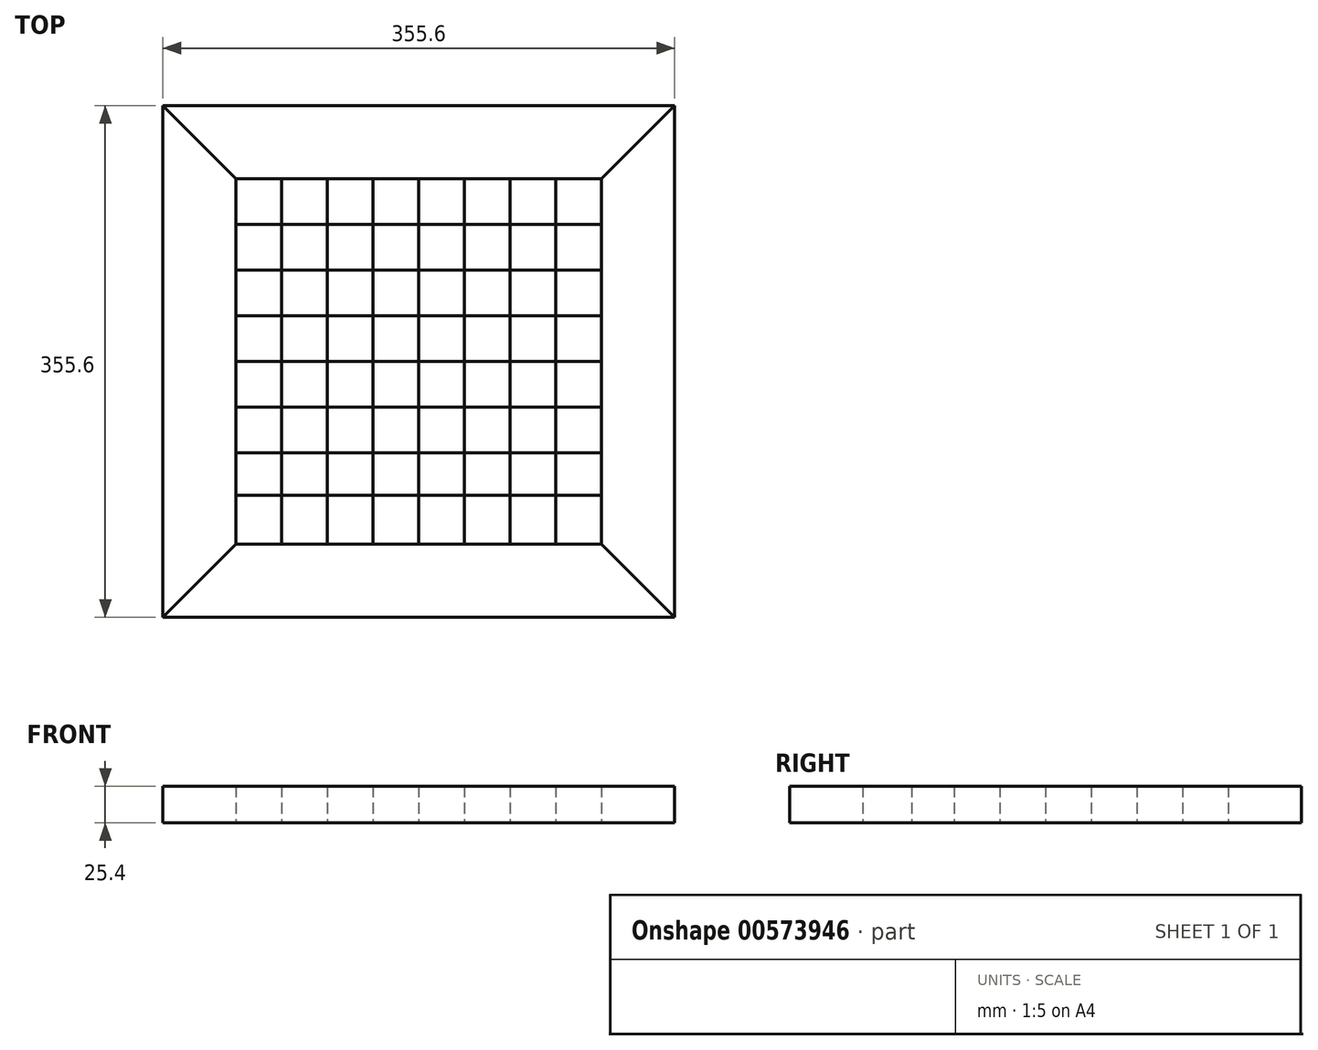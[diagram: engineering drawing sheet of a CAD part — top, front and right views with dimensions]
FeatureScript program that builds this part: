
annotation { "Feature Type Name" : "Feature", "Feature Type Description" : "" }
export const myFeature = defineFeature(function(context is Context, id is Id, definition is map)
    precondition{}
    {
        {
            var Q0;
            Q0=qCreatedBy(makeId("Top.planeOp"),FACE);
            var sketch = newSketch(context, id + "F0", { "sketchPlane" : qUnion([Q0])});
            skLineSegment(sketch, "E0.bottom", {"start": v(-177.8, -177.8) * mm, "end": v(177.8, -177.8) * mm});
            skLineSegment(sketch, "E0.top", {"start": v(-177.8, 177.8) * mm, "end": v(177.8, 177.8) * mm});
            skLineSegment(sketch, "E0.left", {"start": v(-177.8, -177.8) * mm, "end": v(-177.8, 177.8) * mm});
            skLineSegment(sketch, "E0.right", {"start": v(177.8, -177.8) * mm, "end": v(177.8, 177.8) * mm});
            skPoint(sketch, "E0.middle", {"position": v(0, 0) * mm});
            skLineSegment(sketch, "E1", {"start": v(-177.8, 177.8) * mm, "end": v(-127, 127) * mm});
            skLineSegment(sketch, "E2", {"start": v(-177.8, -177.8) * mm, "end": v(-127, -127) * mm});
            skLineSegment(sketch, "E3", {"start": v(-127, 127) * mm, "end": v(-127, -127) * mm});
            skLineSegment(sketch, "E4", {"start": v(-127, 127) * mm, "end": v(127, 127) * mm});
            skLineSegment(sketch, "E5", {"start": v(127, 127) * mm, "end": v(127, -127) * mm});
            skLineSegment(sketch, "E6", {"start": v(127, -127) * mm, "end": v(-127, -127) * mm});
            skLineSegment(sketch, "E7.trimOffspring", {"start": v(127, -127) * mm, "end": v(177.8, -177.8) * mm});
            skLineSegment(sketch, "E8.trimOffspring", {"start": v(127, 127) * mm, "end": v(177.8, 177.8) * mm});
            skLineSegment(sketch, "E9", {"start": v(-95.25, 127) * mm, "end": v(-95.25, -127) * mm});
            skLineSegment(sketch, "E10", {"start": v(-63.5, 127) * mm, "end": v(-63.5, -127) * mm});
            skLineSegment(sketch, "E11", {"start": v(-31.75, 127) * mm, "end": v(-31.75, -127) * mm});
            skLineSegment(sketch, "E12", {"start": v(0, 127) * mm, "end": v(0, -127) * mm});
            skLineSegment(sketch, "E13", {"start": v(31.75, 127) * mm, "end": v(31.75, -127) * mm});
            skLineSegment(sketch, "E14", {"start": v(63.5, 127) * mm, "end": v(63.5, -127) * mm});
            skLineSegment(sketch, "E15", {"start": v(95.25, 127) * mm, "end": v(95.25, -127) * mm});
            skLineSegment(sketch, "E16", {"start": v(-127, 95.25) * mm, "end": v(127, 95.25) * mm});
            skLineSegment(sketch, "E17", {"start": v(-127, 63.5) * mm, "end": v(127, 63.5) * mm});
            skLineSegment(sketch, "E18", {"start": v(-127, 31.75) * mm, "end": v(127, 31.75) * mm});
            skLineSegment(sketch, "E19", {"start": v(-127, 0) * mm, "end": v(127, 0) * mm});
            skLineSegment(sketch, "E20", {"start": v(-127, -31.75) * mm, "end": v(127, -31.75) * mm});
            skLineSegment(sketch, "E21", {"start": v(-127, -63.5) * mm, "end": v(127, -63.5) * mm});
            skLineSegment(sketch, "E22", {"start": v(127, -92.97) * mm, "end": v(-127, -92.97) * mm});
            skSolve(sketch);
        }
        {
            var Q0;
            Q0=makeQuery(id+"F0.imprint","IMPRINT",FACE,{"disambiguationData":[TD([[makeQuery(id+"F0.imprint","IMPRINT",EDGE,{"derivedFrom":sQuery(id+"F0.wireOp",EDGE,"E0.top")}),-1.0]])]});
            var Q1;
            Q1=makeQuery(id+"F0.imprint","IMPRINT",FACE,{"disambiguationData":[TD([[makeQuery(id+"F0.imprint","IMPRINT",EDGE,{"derivedFrom":sQuery(id+"F0.wireOp",EDGE,"E0.bottom")}),1.0]])]});
            extrude(context, id + "F1", {"entities" : qUnion([Q0, Q1]), "depth" : 25.4 * mm, "offsetDistance" : 25.4 * mm});
        }
        {
            var Q0;
            Q0=makeQuery(id+"F0.imprint","IMPRINT",FACE,{"disambiguationData":[TD([[makeQuery(id+"F0.imprint","IMPRINT",EDGE,{"derivedFrom":sQuery(id+"F0.wireOp",EDGE,"E0.left")}),-1.0]])]});
            var Q1;
            Q1=makeQuery(id+"F0.imprint","IMPRINT",FACE,{"disambiguationData":[TD([[makeQuery(id+"F0.imprint","IMPRINT",EDGE,{"derivedFrom":sQuery(id+"F0.wireOp",EDGE,"E0.right")}),1.0]])]});
            extrude(context, id + "F2", {"entities" : qUnion([Q0, Q1]), "depth" : 25.4 * mm, "offsetDistance" : 25.4 * mm});
        }
        {
            var Q0;
            {var subQ0=sQuery(id+"F0.wireOp",EDGE,"E4");var subQ5=sQuery(id+"F0.wireOp",EDGE,"E9");var subQ7=makeQuery(id+"F0.imprint","INTERSECT",VERTEX,{"derivedFrom":[subQ0,subQ5]});Q0=makeQuery(id+"F0.imprint","IMPRINT",FACE,{"disambiguationData":[TD([[makeQuery(id+"F0.imprint","IMPRINT",EDGE,{"disambiguationData":[TD([[subQ7,-1.0]])],"derivedFrom":subQ5}),-1.0]])]});}
            var Q1;
            {var subQ0=sQuery(id+"F0.wireOp",EDGE,"E10");var subQ1=sQuery(id+"F0.wireOp",EDGE,"E4");var subQ2=makeQuery(id+"F0.imprint","INTERSECT",VERTEX,{"derivedFrom":[subQ1,subQ0]});Q1=makeQuery(id+"F0.imprint","IMPRINT",FACE,{"disambiguationData":[TD([[makeQuery(id+"F0.imprint","IMPRINT",EDGE,{"disambiguationData":[TD([[subQ2,-1.0]])],"derivedFrom":subQ1}),-1.0]])]});}
            var Q2;
            {var subQ0=sQuery(id+"F0.wireOp",EDGE,"E12");var subQ1=sQuery(id+"F0.wireOp",EDGE,"E4");var subQ2=makeQuery(id+"F0.imprint","INTERSECT",VERTEX,{"derivedFrom":[subQ1,subQ0]});Q2=makeQuery(id+"F0.imprint","IMPRINT",FACE,{"disambiguationData":[TD([[makeQuery(id+"F0.imprint","IMPRINT",EDGE,{"disambiguationData":[TD([[subQ2,-1.0]])],"derivedFrom":subQ1}),-1.0]])]});}
            var Q3;
            {var subQ0=sQuery(id+"F0.wireOp",EDGE,"E14");var subQ1=sQuery(id+"F0.wireOp",EDGE,"E4");var subQ2=makeQuery(id+"F0.imprint","INTERSECT",VERTEX,{"derivedFrom":[subQ1,subQ0]});Q3=makeQuery(id+"F0.imprint","IMPRINT",FACE,{"disambiguationData":[TD([[makeQuery(id+"F0.imprint","IMPRINT",EDGE,{"disambiguationData":[TD([[subQ2,-1.0]])],"derivedFrom":subQ1}),-1.0]])]});}
            var Q4;
            {var subQ0=sQuery(id+"F0.wireOp",EDGE,"E16");var subQ1=sQuery(id+"F0.wireOp",EDGE,"E13");var subQ2=makeQuery(id+"F0.imprint","INTERSECT",VERTEX,{"derivedFrom":[subQ1,subQ0]});Q4=makeQuery(id+"F0.imprint","IMPRINT",FACE,{"disambiguationData":[TD([[makeQuery(id+"F0.imprint","IMPRINT",EDGE,{"disambiguationData":[TD([[subQ2,-1.0]])],"derivedFrom":subQ1}),1.0]])]});}
            var Q5;
            {var subQ0=sQuery(id+"F0.wireOp",EDGE,"E16");var subQ1=sQuery(id+"F0.wireOp",EDGE,"E11");var subQ2=makeQuery(id+"F0.imprint","INTERSECT",VERTEX,{"derivedFrom":[subQ1,subQ0]});Q5=makeQuery(id+"F0.imprint","IMPRINT",FACE,{"disambiguationData":[TD([[makeQuery(id+"F0.imprint","IMPRINT",EDGE,{"disambiguationData":[TD([[subQ2,-1.0]])],"derivedFrom":subQ1}),1.0]])]});}
            var Q6;
            {var subQ0=sQuery(id+"F0.wireOp",EDGE,"E16");var subQ1=sQuery(id+"F0.wireOp",EDGE,"E9");var subQ2=makeQuery(id+"F0.imprint","INTERSECT",VERTEX,{"derivedFrom":[subQ1,subQ0]});Q6=makeQuery(id+"F0.imprint","IMPRINT",FACE,{"disambiguationData":[TD([[makeQuery(id+"F0.imprint","IMPRINT",EDGE,{"disambiguationData":[TD([[subQ2,-1.0]])],"derivedFrom":subQ1}),1.0]])]});}
            var Q7;
            {var subQ0=sQuery(id+"F0.wireOp",EDGE,"E17");var subQ1=sQuery(id+"F0.wireOp",EDGE,"E3");var subQ2=makeQuery(id+"F0.imprint","INTERSECT",VERTEX,{"derivedFrom":[subQ1,subQ0]});Q7=makeQuery(id+"F0.imprint","IMPRINT",FACE,{"disambiguationData":[TD([[makeQuery(id+"F0.imprint","IMPRINT",EDGE,{"disambiguationData":[TD([[subQ2,-1.0]])],"derivedFrom":subQ1}),1.0]])]});}
            var Q8;
            {var subQ0=sQuery(id+"F0.wireOp",EDGE,"E17");var subQ1=sQuery(id+"F0.wireOp",EDGE,"E10");var subQ2=makeQuery(id+"F0.imprint","INTERSECT",VERTEX,{"derivedFrom":[subQ1,subQ0]});Q8=makeQuery(id+"F0.imprint","IMPRINT",FACE,{"disambiguationData":[TD([[makeQuery(id+"F0.imprint","IMPRINT",EDGE,{"disambiguationData":[TD([[subQ2,-1.0]])],"derivedFrom":subQ1}),1.0]])]});}
            var Q9;
            {var subQ0=sQuery(id+"F0.wireOp",EDGE,"E17");var subQ1=sQuery(id+"F0.wireOp",EDGE,"E12");var subQ2=makeQuery(id+"F0.imprint","INTERSECT",VERTEX,{"derivedFrom":[subQ1,subQ0]});Q9=makeQuery(id+"F0.imprint","IMPRINT",FACE,{"disambiguationData":[TD([[makeQuery(id+"F0.imprint","IMPRINT",EDGE,{"disambiguationData":[TD([[subQ2,-1.0]])],"derivedFrom":subQ1}),1.0]])]});}
            var Q10;
            {var subQ0=sQuery(id+"F0.wireOp",EDGE,"E17");var subQ1=sQuery(id+"F0.wireOp",EDGE,"E14");var subQ2=makeQuery(id+"F0.imprint","INTERSECT",VERTEX,{"derivedFrom":[subQ1,subQ0]});Q10=makeQuery(id+"F0.imprint","IMPRINT",FACE,{"disambiguationData":[TD([[makeQuery(id+"F0.imprint","IMPRINT",EDGE,{"disambiguationData":[TD([[subQ2,-1.0]])],"derivedFrom":subQ1}),1.0]])]});}
            var Q11;
            {var subQ0=sQuery(id+"F0.wireOp",EDGE,"E18");var subQ1=sQuery(id+"F0.wireOp",EDGE,"E13");var subQ2=makeQuery(id+"F0.imprint","INTERSECT",VERTEX,{"derivedFrom":[subQ1,subQ0]});Q11=makeQuery(id+"F0.imprint","IMPRINT",FACE,{"disambiguationData":[TD([[makeQuery(id+"F0.imprint","IMPRINT",EDGE,{"disambiguationData":[TD([[subQ2,-1.0]])],"derivedFrom":subQ1}),1.0]])]});}
            var Q12;
            {var subQ0=sQuery(id+"F0.wireOp",EDGE,"E18");var subQ1=sQuery(id+"F0.wireOp",EDGE,"E11");var subQ2=makeQuery(id+"F0.imprint","INTERSECT",VERTEX,{"derivedFrom":[subQ1,subQ0]});Q12=makeQuery(id+"F0.imprint","IMPRINT",FACE,{"disambiguationData":[TD([[makeQuery(id+"F0.imprint","IMPRINT",EDGE,{"disambiguationData":[TD([[subQ2,-1.0]])],"derivedFrom":subQ1}),1.0]])]});}
            var Q13;
            {var subQ0=sQuery(id+"F0.wireOp",EDGE,"E18");var subQ1=sQuery(id+"F0.wireOp",EDGE,"E9");var subQ2=makeQuery(id+"F0.imprint","INTERSECT",VERTEX,{"derivedFrom":[subQ1,subQ0]});Q13=makeQuery(id+"F0.imprint","IMPRINT",FACE,{"disambiguationData":[TD([[makeQuery(id+"F0.imprint","IMPRINT",EDGE,{"disambiguationData":[TD([[subQ2,-1.0]])],"derivedFrom":subQ1}),1.0]])]});}
            var Q14;
            {var subQ0=sQuery(id+"F0.wireOp",EDGE,"E19");var subQ1=sQuery(id+"F0.wireOp",EDGE,"E3");var subQ2=makeQuery(id+"F0.imprint","INTERSECT",VERTEX,{"derivedFrom":[subQ1,subQ0]});Q14=makeQuery(id+"F0.imprint","IMPRINT",FACE,{"disambiguationData":[TD([[makeQuery(id+"F0.imprint","IMPRINT",EDGE,{"disambiguationData":[TD([[subQ2,-1.0]])],"derivedFrom":subQ1}),1.0]])]});}
            var Q15;
            {var subQ0=sQuery(id+"F0.wireOp",EDGE,"E19");var subQ1=sQuery(id+"F0.wireOp",EDGE,"E10");var subQ2=makeQuery(id+"F0.imprint","INTERSECT",VERTEX,{"derivedFrom":[subQ1,subQ0]});Q15=makeQuery(id+"F0.imprint","IMPRINT",FACE,{"disambiguationData":[TD([[makeQuery(id+"F0.imprint","IMPRINT",EDGE,{"disambiguationData":[TD([[subQ2,-1.0]])],"derivedFrom":subQ1}),1.0]])]});}
            var Q16;
            {var subQ0=sQuery(id+"F0.wireOp",EDGE,"E19");var subQ1=sQuery(id+"F0.wireOp",EDGE,"E12");var subQ2=makeQuery(id+"F0.imprint","INTERSECT",VERTEX,{"derivedFrom":[subQ1,subQ0]});Q16=makeQuery(id+"F0.imprint","IMPRINT",FACE,{"disambiguationData":[TD([[makeQuery(id+"F0.imprint","IMPRINT",EDGE,{"disambiguationData":[TD([[subQ2,-1.0]])],"derivedFrom":subQ1}),1.0]])]});}
            var Q17;
            {var subQ0=sQuery(id+"F0.wireOp",EDGE,"E19");var subQ1=sQuery(id+"F0.wireOp",EDGE,"E14");var subQ2=makeQuery(id+"F0.imprint","INTERSECT",VERTEX,{"derivedFrom":[subQ1,subQ0]});Q17=makeQuery(id+"F0.imprint","IMPRINT",FACE,{"disambiguationData":[TD([[makeQuery(id+"F0.imprint","IMPRINT",EDGE,{"disambiguationData":[TD([[subQ2,-1.0]])],"derivedFrom":subQ1}),1.0]])]});}
            var Q18;
            {var subQ0=sQuery(id+"F0.wireOp",EDGE,"E20");var subQ1=sQuery(id+"F0.wireOp",EDGE,"E13");var subQ2=makeQuery(id+"F0.imprint","INTERSECT",VERTEX,{"derivedFrom":[subQ1,subQ0]});Q18=makeQuery(id+"F0.imprint","IMPRINT",FACE,{"disambiguationData":[TD([[makeQuery(id+"F0.imprint","IMPRINT",EDGE,{"disambiguationData":[TD([[subQ2,-1.0]])],"derivedFrom":subQ1}),1.0]])]});}
            var Q19;
            {var subQ0=sQuery(id+"F0.wireOp",EDGE,"E20");var subQ1=sQuery(id+"F0.wireOp",EDGE,"E11");var subQ2=makeQuery(id+"F0.imprint","INTERSECT",VERTEX,{"derivedFrom":[subQ1,subQ0]});Q19=makeQuery(id+"F0.imprint","IMPRINT",FACE,{"disambiguationData":[TD([[makeQuery(id+"F0.imprint","IMPRINT",EDGE,{"disambiguationData":[TD([[subQ2,-1.0]])],"derivedFrom":subQ1}),1.0]])]});}
            var Q20;
            {var subQ0=sQuery(id+"F0.wireOp",EDGE,"E20");var subQ1=sQuery(id+"F0.wireOp",EDGE,"E9");var subQ2=makeQuery(id+"F0.imprint","INTERSECT",VERTEX,{"derivedFrom":[subQ1,subQ0]});Q20=makeQuery(id+"F0.imprint","IMPRINT",FACE,{"disambiguationData":[TD([[makeQuery(id+"F0.imprint","IMPRINT",EDGE,{"disambiguationData":[TD([[subQ2,-1.0]])],"derivedFrom":subQ1}),1.0]])]});}
            var Q21;
            {var subQ0=sQuery(id+"F0.wireOp",EDGE,"E21");var subQ1=sQuery(id+"F0.wireOp",EDGE,"E3");var subQ2=makeQuery(id+"F0.imprint","INTERSECT",VERTEX,{"derivedFrom":[subQ1,subQ0]});Q21=makeQuery(id+"F0.imprint","IMPRINT",FACE,{"disambiguationData":[TD([[makeQuery(id+"F0.imprint","IMPRINT",EDGE,{"disambiguationData":[TD([[subQ2,-1.0]])],"derivedFrom":subQ1}),1.0]])]});}
            var Q22;
            {var subQ0=sQuery(id+"F0.wireOp",EDGE,"E21");var subQ1=sQuery(id+"F0.wireOp",EDGE,"E10");var subQ2=makeQuery(id+"F0.imprint","INTERSECT",VERTEX,{"derivedFrom":[subQ1,subQ0]});Q22=makeQuery(id+"F0.imprint","IMPRINT",FACE,{"disambiguationData":[TD([[makeQuery(id+"F0.imprint","IMPRINT",EDGE,{"disambiguationData":[TD([[subQ2,-1.0]])],"derivedFrom":subQ1}),1.0]])]});}
            var Q23;
            {var subQ0=sQuery(id+"F0.wireOp",EDGE,"E21");var subQ1=sQuery(id+"F0.wireOp",EDGE,"E12");var subQ2=makeQuery(id+"F0.imprint","INTERSECT",VERTEX,{"derivedFrom":[subQ1,subQ0]});Q23=makeQuery(id+"F0.imprint","IMPRINT",FACE,{"disambiguationData":[TD([[makeQuery(id+"F0.imprint","IMPRINT",EDGE,{"disambiguationData":[TD([[subQ2,-1.0]])],"derivedFrom":subQ1}),1.0]])]});}
            var Q24;
            {var subQ0=sQuery(id+"F0.wireOp",EDGE,"E21");var subQ1=sQuery(id+"F0.wireOp",EDGE,"E14");var subQ2=makeQuery(id+"F0.imprint","INTERSECT",VERTEX,{"derivedFrom":[subQ1,subQ0]});Q24=makeQuery(id+"F0.imprint","IMPRINT",FACE,{"disambiguationData":[TD([[makeQuery(id+"F0.imprint","IMPRINT",EDGE,{"disambiguationData":[TD([[subQ2,-1.0]])],"derivedFrom":subQ1}),1.0]])]});}
            var Q25;
            {var subQ0=sQuery(id+"F0.wireOp",EDGE,"E13");var subQ1=sQuery(id+"F0.wireOp",EDGE,"E6");var subQ2=makeQuery(id+"F0.imprint","INTERSECT",VERTEX,{"derivedFrom":[subQ1,subQ0]});Q25=makeQuery(id+"F0.imprint","IMPRINT",FACE,{"disambiguationData":[TD([[makeQuery(id+"F0.imprint","IMPRINT",EDGE,{"disambiguationData":[TD([[subQ2,1.0]])],"derivedFrom":subQ1}),-1.0]])]});}
            var Q26;
            {var subQ0=sQuery(id+"F0.wireOp",EDGE,"E11");var subQ1=sQuery(id+"F0.wireOp",EDGE,"E6");var subQ2=makeQuery(id+"F0.imprint","INTERSECT",VERTEX,{"derivedFrom":[subQ1,subQ0]});Q26=makeQuery(id+"F0.imprint","IMPRINT",FACE,{"disambiguationData":[TD([[makeQuery(id+"F0.imprint","IMPRINT",EDGE,{"disambiguationData":[TD([[subQ2,1.0]])],"derivedFrom":subQ1}),-1.0]])]});}
            var Q27;
            {var subQ0=sQuery(id+"F0.wireOp",EDGE,"E9");var subQ1=sQuery(id+"F0.wireOp",EDGE,"E6");var subQ2=makeQuery(id+"F0.imprint","INTERSECT",VERTEX,{"derivedFrom":[subQ1,subQ0]});Q27=makeQuery(id+"F0.imprint","IMPRINT",FACE,{"disambiguationData":[TD([[makeQuery(id+"F0.imprint","IMPRINT",EDGE,{"disambiguationData":[TD([[subQ2,1.0]])],"derivedFrom":subQ1}),-1.0]])]});}
            var Q28;
            {var subQ0=sQuery(id+"F0.wireOp",EDGE,"E16");var subQ1=sQuery(id+"F0.wireOp",EDGE,"E5");var subQ2=makeQuery(id+"F0.imprint","INTERSECT",VERTEX,{"derivedFrom":[subQ1,subQ0]});Q28=makeQuery(id+"F0.imprint","IMPRINT",FACE,{"disambiguationData":[TD([[makeQuery(id+"F0.imprint","IMPRINT",EDGE,{"disambiguationData":[TD([[subQ2,-1.0]])],"derivedFrom":subQ1}),-1.0]])]});}
            var Q29;
            {var subQ0=sQuery(id+"F0.wireOp",EDGE,"E18");var subQ1=sQuery(id+"F0.wireOp",EDGE,"E5");var subQ2=makeQuery(id+"F0.imprint","INTERSECT",VERTEX,{"derivedFrom":[subQ1,subQ0]});Q29=makeQuery(id+"F0.imprint","IMPRINT",FACE,{"disambiguationData":[TD([[makeQuery(id+"F0.imprint","IMPRINT",EDGE,{"disambiguationData":[TD([[subQ2,-1.0]])],"derivedFrom":subQ1}),-1.0]])]});}
            var Q30;
            {var subQ0=sQuery(id+"F0.wireOp",EDGE,"E20");var subQ1=sQuery(id+"F0.wireOp",EDGE,"E5");var subQ2=makeQuery(id+"F0.imprint","INTERSECT",VERTEX,{"derivedFrom":[subQ1,subQ0]});Q30=makeQuery(id+"F0.imprint","IMPRINT",FACE,{"disambiguationData":[TD([[makeQuery(id+"F0.imprint","IMPRINT",EDGE,{"disambiguationData":[TD([[subQ2,-1.0]])],"derivedFrom":subQ1}),-1.0]])]});}
            var Q31;
            {var subQ0=sQuery(id+"F0.wireOp",EDGE,"E6");var subQ5=sQuery(id+"F0.wireOp",EDGE,"E15");var subQ7=makeQuery(id+"F0.imprint","INTERSECT",VERTEX,{"derivedFrom":[subQ0,subQ5]});Q31=makeQuery(id+"F0.imprint","IMPRINT",FACE,{"disambiguationData":[TD([[makeQuery(id+"F0.imprint","IMPRINT",EDGE,{"disambiguationData":[TD([[subQ7,1.0]])],"derivedFrom":subQ5}),1.0]])]});}
            extrude(context, id + "F3", {"entities" : qUnion([Q0, Q1, Q2, Q3, Q4, Q5, Q6, Q7, Q8, Q9, Q10, Q11, Q12, Q13, Q14, Q15, Q16, Q17, Q18, Q19, Q20, Q21, Q22, Q23, Q24, Q25, Q26, Q27, Q28, Q29, Q30, Q31]), "depth" : 25.4 * mm, "offsetDistance" : 25.4 * mm});
        }
    });
